# Revit family: Hager-Typ.B_TP&N_125A_Side_DIN_Enclosures-syst-NoHosted-UK-en
name_source: partatom
category: Electrical Equipment
units: mm (PartAtom-declared; Revit-internal decimal feet)

## family parameters
Always vertical = Yes
Cut with Voids When Loaded = No
Panel Configuration = Two Columns, Circuits Across
Part Type = Panelboard
Room Calculation Point = No
Round Connector Dimension = Use Diameter
Shared = No
Work Plane-Based = Yes

## types (10) — shared parameters
Default Elevation = 1219 mm
EF000003 - Mounting method = EV000384 - Surface mounted (plaster)
EF000008 - Width = 465 mm  [stored 1.52559 ft]
EF000049 - Depth = 132 mm  [stored 0.433071 ft]
EF000118 - With mounting plate = No
EF000339 - Type of cover = EV004216 - Door
EF001062 - EMC-version = No
EF001134 - DIN-rail = No
EF001596 - Material housing = EV000179 - Steel
EF004462 - Type of closure = EV000154 - Other
EF006244 - Transparent cover/door = Yes
EF015776 - Earthing terminal block = Yes
EF015777 - Neutral terminal block = Yes
EF015941 - Signal passing door = No
HG000001 - Number of columns = 1
HG000002 - With door or cover = Yes
HG000003 - Range = Type B TP&N Distribution Boards
HG000005 - Thickness = 3 mm  [stored 0.00984252 ft]
HG000006 - Flush mounted = No
HG000009 - Double swing door = No
HG000010 - Asymmetric doors = No
HG000011 - Empty rows from bottom = No
HG000017 - Distance between poles = 18 mm  [stored 0.0590551 ft]
Manufacturer = Hager
Type Comments = Type B TP&N Distribution Boards
zero-valued in all types: EF000218 - Built-in depth, EF000332 - Built-in height, EF000846 - Built-in width, EF001131 - Internal depth, HG000007 - Number of empty columns, HG000008 - Number of empty rows

## per-type parameters (varying)
| type | EF000007 - Colour | EF000040 - Height | EF000116 - RAL-number | EF000266 - Number of rows | EF001088 - Extension possible | EF002950 - Width in number of modular spacings | EF005474 - Degree of protection (IP) | EF006306 - With lock | HG000004 - Manufacturer reference | Model |
| Surface mounted IP30 W465 H500 D132.5 16 Modular spacings - JK104BDFA3 |  | 500 mm  [stored 1.64042 ft] | 7035 | 2 | Yes | 16 | EV006410 - IP30 | No | JK104BDFA3 | JK104BDFA3 |
| Surface mounted IP30 W465 H550 D132.5 16 Modular spacings - JK106BDFA3 |  | 550 mm | 7035 | 2 | Yes | 16 | EV006410 - IP30 | No | JK106BDFA3 | JK106BDFA3 |
| Surface mounted IP30 W465 H625 D132.5 16 Modular spacings - JK108BDFA3 |  | 625 mm  [stored 2.05052 ft] | 7035 | 3 | Yes | 16 | EV006410 - IP30 | No | JK108BDFA3 | JK108BDFA3 |
| Surface mounted IP30 W465 H850 D132.5 16 Modular spacings - JK112BDFA3 |  | 850 mm  [stored 2.78871 ft] | 7035 | 4 | Yes | 16 | EV006410 - IP30 | No | JK112BDFA3 | JK112BDFA3 |
| Surface mounted IP30 W465 H950 D132.5 16 Modular spacings - JK116BDFA3 |  | 950 mm  [stored 3.1168 ft] | 7035 | 5 | Yes | 16 | EV006410 - IP30 | No | JK116BDFA3 | JK116BDFA3 |
| Surface mounted IP30 W465 H950 D132.5 16 Modular spacings - JK116BDFG | EV000154 - Other | 950 mm  [stored 3.1168 ft] |  | 5 | No | 16 | EV006410 - IP30 | Yes | JK116BDFG | JK116BDFG |
| Surface mounted IP3X W465 H500 D132.5 16 Modular spacings - JK104BDFG | EV000154 - Other | 500 mm  [stored 1.64042 ft] |  | 2 | No | 16 | EV006414 - IP3X | Yes | JK104BDFG | JK104BDFG |
| Surface mounted IP3X W465 H550 D132.5 16 Modular spacings - JK106BDFG | EV000154 - Other | 550 mm |  | 2 | No | 16 | EV006414 - IP3X | Yes | JK106BDFG | JK106BDFG |
| Surface mounted IP3X W465 H625 D132.5 48 Modular spacings - JK108BDFG | EV000154 - Other | 625 mm  [stored 2.05052 ft] |  | 3 | No | 48 | EV006414 - IP3X | Yes | JK108BDFG | JK108BDFG |
| Surface mounted IP3X W465 H850 D132.5 64 Modular spacings - JK112BDFG | EV000154 - Other | 850 mm  [stored 2.78871 ft] |  | 4 | No | 64 | EV006414 - IP3X | Yes | JK112BDFG | JK112BDFG |

note: [stored X ft] marks values corroborated as IEEE doubles in the binary element streams (Revit-internal decimal feet)

## geometry (parser evidence)
native form markers: Sweep x14
no freeform markers — native parametric forms only
